FCSTD DOCUMENT  (FreeCAD 0.16R6712 (Git))
Label: Idler Bolt Clamp
License: All rights reserved
LicenseURL: http://en.wikipedia.org/wiki/All_rights_reserved
objects: Sketcher::SketchObject×1
note: 1 computed .brp shape members not serialized (recipe doc carries the construction recipe); baked Part::Feature solids carry a one-line shape summary decoded from their .brp

FEATURE [Sketcher::SketchObject] Sketch
  Placement = pos=(0,0,-76.2) rot=(1,0,0;3.14159rad)
  sketch-geometry (17):
    g0: Circle CenterX=0 CenterY=0 CenterZ=0 NormalX=0 NormalY=0 NormalZ=1 Radius=50.8
    g1: ArcOfCircle CenterX=0 CenterY=0 CenterZ=0 NormalX=0 NormalY=0 NormalZ=1 Radius=62.5546 StartAngle=6.17749 EndAngle=6.38888
    g2: LineSegment StartX=-62.2055 StartY=6.5996 StartZ=0 EndX=-108.014 EndY=6.5996 EndZ=0
    g3: LineSegment StartX=-108.014 StartY=6.5996 StartZ=0 EndX=-108.014 EndY=16.8465 EndZ=0
    g4: LineSegment StartX=-108.014 StartY=16.8465 StartZ=0 EndX=-60.2435 EndY=16.8465 EndZ=0
    g5: LineSegment StartX=-62.2055 StartY=-6.5996 StartZ=0 EndX=-108.014 EndY=-6.5996 EndZ=0
    g6: LineSegment StartX=-108.014 StartY=-6.5996 StartZ=0 EndX=-108.014 EndY=-16.8465 EndZ=0
    g7: LineSegment StartX=-108.014 StartY=-16.8465 StartZ=0 EndX=-60.2435 EndY=-16.8465 EndZ=0
    g8: LineSegment StartX=62.2055 StartY=6.5996 StartZ=0 EndX=108.014 EndY=6.5996 EndZ=0
    g9: LineSegment StartX=108.014 StartY=6.5996 StartZ=0 EndX=108.014 EndY=16.8465 EndZ=0
    g10: LineSegment StartX=108.014 StartY=16.8465 StartZ=0 EndX=60.2435 EndY=16.8465 EndZ=0
    g11: LineSegment StartX=62.2055 StartY=-6.5996 StartZ=0 EndX=108.014 EndY=-6.5996 EndZ=0
    g12: LineSegment StartX=108.014 StartY=-6.5996 StartZ=0 EndX=108.014 EndY=-16.8465 EndZ=0
    g13: LineSegment StartX=108.014 StartY=-16.8465 StartZ=0 EndX=60.2435 EndY=-16.8465 EndZ=0
    g14: ArcOfCircle CenterX=0 CenterY=0 CenterZ=0 NormalX=0 NormalY=0 NormalZ=1 Radius=62.5546 StartAngle=3.03589 EndAngle=3.24729
    g15: ArcOfCircle CenterX=0 CenterY=0 CenterZ=0 NormalX=0 NormalY=0 NormalZ=1 Radius=62.5546 StartAngle=0.272676 EndAngle=2.86892
    g16: ArcOfCircle CenterX=0 CenterY=0 CenterZ=0 NormalX=0 NormalY=0 NormalZ=1 Radius=62.5546 StartAngle=3.41427 EndAngle=6.01051
  constraints (60):
    c: Coincident(g0,g-1)
    c: Radius(g0) = 50.8
    c: Coincident(g1,g-1)
    c: Horizontal(g2)
    c: Coincident(g3,g2)
    c: Coincident(g4,g3)
    c: Horizontal(g4)
    c: Horizontal(g5)
    c: Coincident(g6,g5)
    c: Vertical(g6)
    c: Coincident(g7,g6)
    c: PointOnObject(g7,g1)
    c: Horizontal(g7)
    c: Equal(g6,g3)
    c: Symmetric(g6,g3,g-1)
    c: DistanceX(g7,g7) = 47.7703
    c: DistanceY(g3,g3) = 10.2469
    c: Equal(g7,g4)
    c: Equal(g2,g5)
    c: Horizontal(g8)
    c: Coincident(g9,g8)
    c: Vertical(g9)
    c: Coincident(g10,g9)
    c: PointOnObject(g10,g1)
    c: Horizontal(g10)
    c: Horizontal(g11)
    c: Coincident(g12,g11)
    c: Vertical(g12)
    c: Coincident(g13,g12)
    c: PointOnObject(g13,g1)
    c: Horizontal(g13)
    c: Equal(g12,g9)
    c: Equal(g9,g3)
    c: Equal(g10,g13)
    c: Equal(g13,g7)
    c: Equal(g8,g11)
    c: Equal(g11,g2)
    c: Symmetric(g3,g9,g-2)
    c: Symmetric(g9,g12,g-1)
    c: Coincident(g1,g11)
    c: Coincident(g14,g5)
    c: Coincident(g1,g8)
    c: Coincident(g14,g2)
    c: Coincident(g1,g14)
    c: Coincident(g15,g-1)
    c: Coincident(g15,g4)
    c: Coincident(g15,g10)
    c: Coincident(g16,g-1)
    c: Coincident(g16,g7)
    c: Coincident(g16,g13)
    c: Radius(g16) = 62.5546
    c: Equal(g16,g14)
    c: Equal(g16,g15)
    c: Symmetric(g4,g7,g-1)
    c: Symmetric(g1,g2,g-2)
    c: Symmetric(g10,g4,g-2)
    c: Symmetric(g1,g5,g-2)
    c: Symmetric(g7,g13,g-2)
    c: Symmetric(g10,g13,g-1)
    c: DistanceX(g10) = 60.2435
